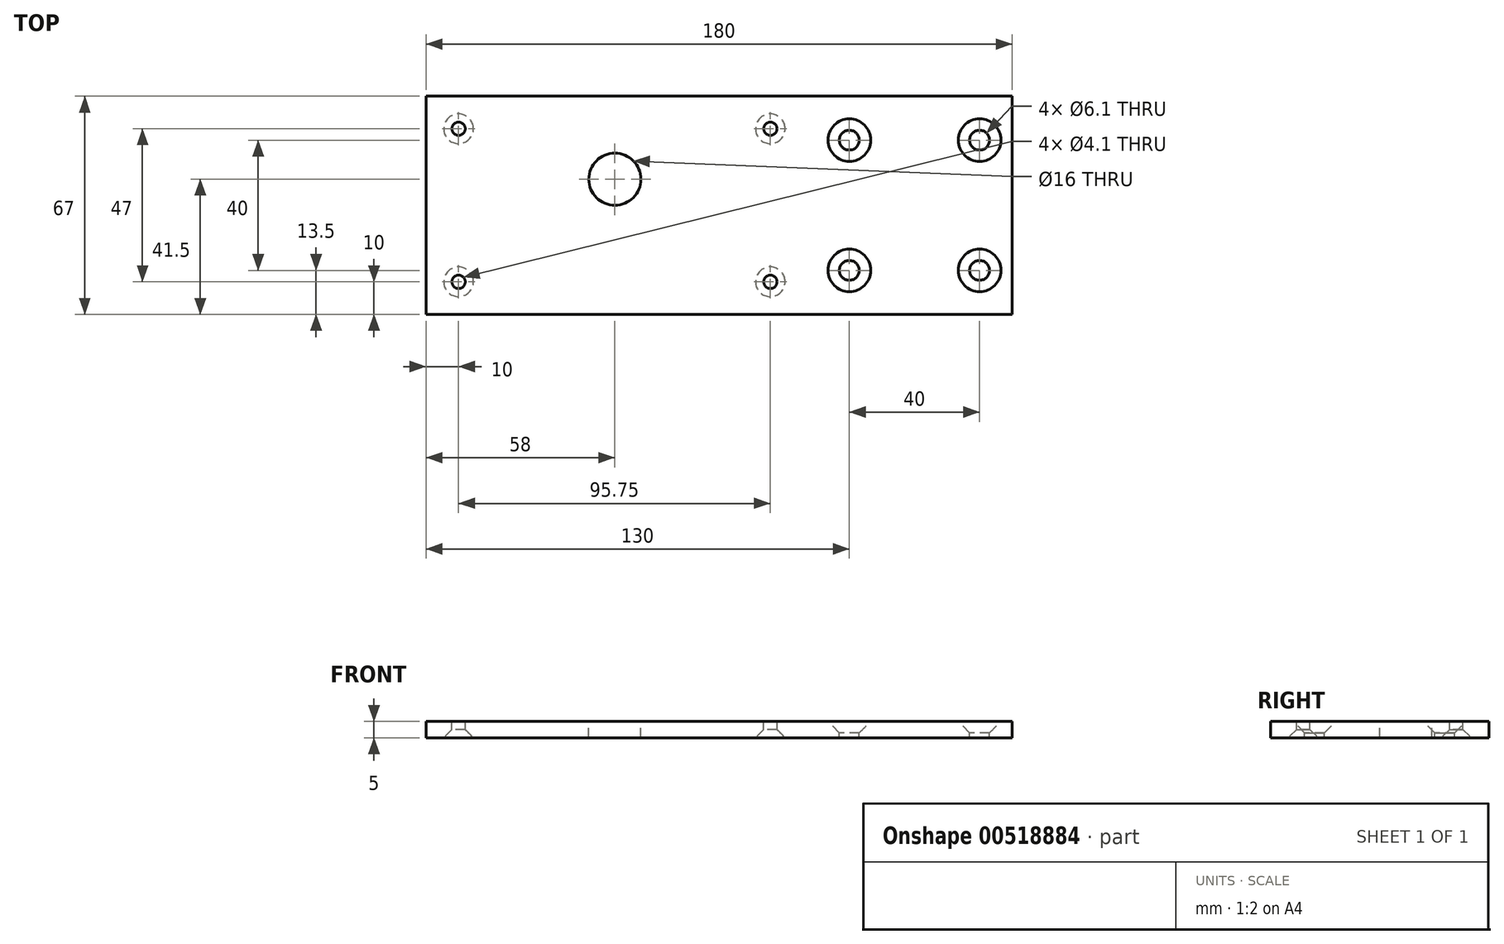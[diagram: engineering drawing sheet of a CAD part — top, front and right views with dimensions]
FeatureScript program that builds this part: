
annotation { "Feature Type Name" : "Feature", "Feature Type Description" : "" }
export const myFeature = defineFeature(function(context is Context, id is Id, definition is map)
    precondition{}
    {
        {
            var Q0;
            Q0=qCreatedBy(makeId("Top.planeOp"),FACE);
            var sketch = newSketch(context, id + "F0", { "sketchPlane" : qUnion([Q0])});
            skLineSegment(sketch, "E0.bottom", {"start": v(0, 0) * mm, "end": v(180, 0) * mm});
            skLineSegment(sketch, "E0.top", {"start": v(0, 67) * mm, "end": v(180, 67) * mm});
            skLineSegment(sketch, "E0.left", {"start": v(0, 0) * mm, "end": v(0, 67) * mm});
            skLineSegment(sketch, "E0.right", {"start": v(180, 0) * mm, "end": v(180, 67) * mm});
            skCircle(sketch, "E1", {"center": v(10, 57) * mm, "radius": 2.05 * mm});
            skCircle(sketch, "E2", {"center": v(10, 10) * mm, "radius": 2.05 * mm});
            skCircle(sketch, "E3", {"center": v(105.75, 57) * mm, "radius": 2.05 * mm});
            skCircle(sketch, "E4", {"center": v(105.75, 10) * mm, "radius": 2.05 * mm});
            skCircle(sketch, "E5", {"center": v(58, 41.5) * mm, "radius": 8 * mm});
            skCircle(sketch, "E6", {"center": v(130, 53.5) * mm, "radius": 3.05 * mm});
            skCircle(sketch, "E7", {"center": v(130, 13.5) * mm, "radius": 3.05 * mm});
            skCircle(sketch, "E8", {"center": v(170, 53.5) * mm, "radius": 3.05 * mm});
            skCircle(sketch, "E9", {"center": v(170, 13.5) * mm, "radius": 3.05 * mm});
            skSolve(sketch);
        }
        {
            var Q0;
            Q0=makeQuery(id+"F0.imprint","IMPRINT",FACE,{"disambiguationData":[TD([[makeQuery(id+"F0.imprint","IMPRINT",EDGE,{"derivedFrom":sQuery(id+"F0.wireOp",EDGE,"E0.bottom")}),1.0]])]});
            extrude(context, id + "F1", {"entities" : qUnion([Q0]), "oppositeDirection" : true, "depth" : 5 * mm, "offsetDistance" : 25 * mm});
        }
        {
            var Q0;
            Q0=makeQuery(id+"F1.opExtrude","CAP_EDGE",EDGE,{"disambiguationData":[OSD([sQuery(id+"F0.wireOp",EDGE,"E6")])],"isStart":true});
            var Q1;
            Q1=makeQuery(id+"F1.opExtrude","CAP_EDGE",EDGE,{"disambiguationData":[OSD([sQuery(id+"F0.wireOp",EDGE,"E8")])],"isStart":true});
            var Q2;
            Q2=makeQuery(id+"F1.opExtrude","CAP_EDGE",EDGE,{"disambiguationData":[OSD([sQuery(id+"F0.wireOp",EDGE,"E9")])],"isStart":true});
            var Q3;
            Q3=makeQuery(id+"F1.opExtrude","CAP_EDGE",EDGE,{"disambiguationData":[OSD([sQuery(id+"F0.wireOp",EDGE,"E7")])],"isStart":true});
            chamfer(context, id + "F2", {"entities" : qUnion([Q0, Q1, Q2, Q3]), "width" : 3.5 * mm, "tangentPropagation" : true});
        }
        {
            var Q0;
            Q0=makeQuery(id+"F1.opExtrude","CAP_EDGE",EDGE,{"disambiguationData":[OSD([sQuery(id+"F0.wireOp",EDGE,"E3")])],"isStart":false});
            var Q1;
            Q1=makeQuery(id+"F1.opExtrude","CAP_EDGE",EDGE,{"disambiguationData":[OSD([sQuery(id+"F0.wireOp",EDGE,"E4")])],"isStart":false});
            var Q2;
            Q2=makeQuery(id+"F1.opExtrude","CAP_EDGE",EDGE,{"disambiguationData":[OSD([sQuery(id+"F0.wireOp",EDGE,"E2")])],"isStart":false});
            var Q3;
            Q3=makeQuery(id+"F1.opExtrude","CAP_EDGE",EDGE,{"disambiguationData":[OSD([sQuery(id+"F0.wireOp",EDGE,"E1")])],"isStart":false});
            chamfer(context, id + "F3", {"entities" : qUnion([Q0, Q1, Q2, Q3]), "width" : 2.5 * mm, "tangentPropagation" : true});
        }
    });
